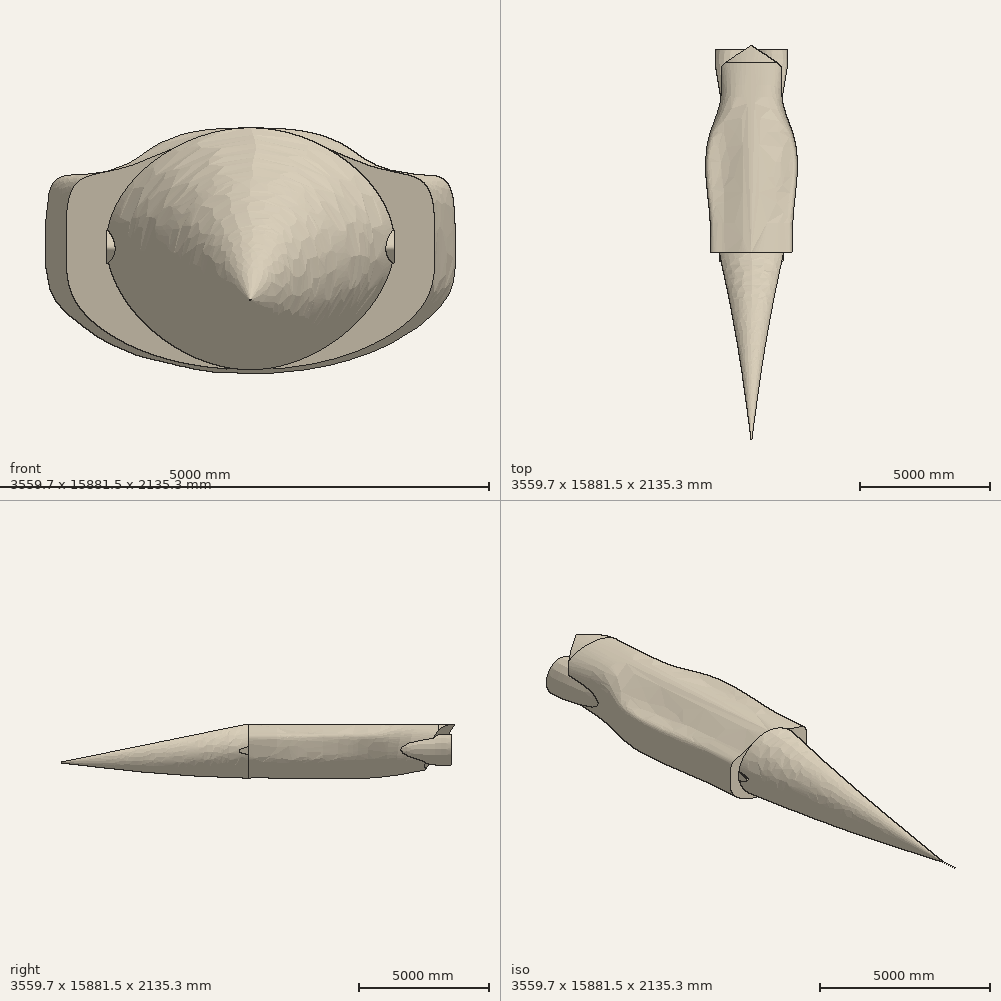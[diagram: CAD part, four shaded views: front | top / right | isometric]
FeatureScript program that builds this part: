
annotation { "Feature Type Name" : "Feature", "Feature Type Description" : "" }
export const myFeature = defineFeature(function(context is Context, id is Id, definition is map)
    precondition{}
    {
        {
            var Q0;
            Q0=qCreatedBy(makeId("Right.planeOp"),FACE);
            var sketch = newSketch(context, id + "F0", { "sketchPlane" : qUnion([Q0])});
            skLineSegment(sketch, "E0", {"start": v(0, 0) * mm, "end": v(-1750, 0) * mm});
            skLineSegment(sketch, "E1", {"start": v(-1750, 0) * mm, "end": v(-3500, 0) * mm});
            skLineSegment(sketch, "E2", {"start": v(-3500, 0) * mm, "end": v(-3500, -1000) * mm});
            skLineSegment(sketch, "E3", {"start": v(-3500, -1000) * mm, "end": v(-8500, -1000) * mm});
            skLineSegment(sketch, "E4", {"start": v(-8500, -1000) * mm, "end": v(-8500, -499.31) * mm});
            skLineSegment(sketch, "E5", {"start": v(-1151.4, 0) * mm, "end": v(-1151.4, 1000) * mm});
            skLineSegment(sketch, "E6", {"start": v(-1151.4, 1000) * mm, "end": v(-8500, -499.31) * mm});
            skLineSegment(sketch, "E7", {"start": v(-8500, -499.31) * mm, "end": v(-3500, -1000) * mm});
            skLineSegment(sketch, "E8", {"start": v(-3500, 0) * mm, "end": v(-3500, 520.82) * mm});
            skLineSegment(sketch, "E9", {"start": v(-8500, -499.31) * mm, "end": v(-8450, -499.31) * mm});
            skLineSegment(sketch, "E10", {"start": v(-8450, -499.31) * mm, "end": v(-8450, -489.1) * mm});
            skLineSegment(sketch, "E11", {"start": v(-8450, -499.31) * mm, "end": v(-8450, -504.32) * mm});
            skSolve(sketch);
        }
        {
            var Q0;
            Q0=sQuery(id+"F0.wireOp",EDGE,"E5");
            cPlane(context, id + "F1", {"entities" : qUnion([Q0]), "cplaneType" : CPlaneType.LINE_ANGLE, "offset" : 25 * mm, "angle" : 90 * degree, "oppositeDirection" : true, "width" : 150 * mm, "height" : 150 * mm});
        }
        {
            var Q0;
            Q0=qCreatedBy(id+"F1.planeOp",FACE);
            var sketch = newSketch(context, id + "F2", { "sketchPlane" : qUnion([Q0])});
            skPoint(sketch, "E12.middle", {"position": v(0, 0) * mm});
            skFitSpline(sketch, "E13", {"points": [v(0, 1000) * mm, v(-1060, 662.5) * mm, v(-1517.6, 506.84) * mm, v(-1600, 0) * mm, v(-1517.6, -506.84) * mm, v(-750, -1000) * mm, v(750, -1000) * mm, v(1517.6, -506.84) * mm, v(1600, 0) * mm, v(1517.6, 506.84) * mm, v(1060, 662.5) * mm, v(0, 1000) * mm]});
            skSolve(sketch);
        }
        {
            var Q0;
            Q0=qCreatedBy(makeId("Front.planeOp"),FACE);
            var sketch = newSketch(context, id + "F3", { "sketchPlane" : qUnion([Q0])});
            skPoint(sketch, "E14.middle", {"position": v(0, 0) * mm});
            skFitSpline(sketch, "E15", {"points": [v(0, 1000) * mm, v(-1060, 662.5) * mm, v(-1517.6, 506.84) * mm, v(-1600, 0) * mm, v(-1517.6, -506.84) * mm, v(-750, -1000) * mm, v(750, -1000) * mm, v(1517.6, -506.84) * mm, v(1600, 0) * mm, v(1517.6, 506.84) * mm, v(1060, 662.5) * mm, v(0, 1000) * mm]});
            skSolve(sketch);
        }
        {
            var Q0;
            Q0=qCreatedBy(makeId("Front.planeOp"),FACE);
            cPlane(context, id + "F4", {"entities" : qUnion([Q0]), "cplaneType" : CPlaneType.OFFSET, "offset" : 3500 * mm, "oppositeDirection" : true, "width" : 150 * mm, "height" : 150 * mm});
        }
        {
            var Q0;
            Q0=qCreatedBy(id+"F4.planeOp",FACE);
            var sketch = newSketch(context, id + "F5", { "sketchPlane" : qUnion([Q0])});
            skPoint(sketch, "E16.middle", {"position": v(0, 0) * mm});
            skFitSpline(sketch, "E17", {"points": [v(0, 1000) * mm, v(-1060, 662.5) * mm, v(-1517.6, 506.84) * mm, v(-1600, 0) * mm, v(-1517.6, -506.84) * mm, v(-750, -1000) * mm, v(750, -1000) * mm, v(1517.6, -506.84) * mm, v(1600, 0) * mm, v(1517.6, 506.84) * mm, v(1060, 662.5) * mm, v(0, 1000) * mm]});
            skSolve(sketch);
        }
        {
            var Q0;
            Q0=qCreatedBy(makeId("Front.planeOp"),FACE);
            cPlane(context, id + "F6", {"entities" : qUnion([Q0]), "cplaneType" : CPlaneType.OFFSET, "offset" : 4500 * mm, "oppositeDirection" : true, "width" : 150 * mm, "height" : 150 * mm});
        }
        {
            var Q0;
            Q0=qCreatedBy(id+"F6.planeOp",FACE);
            var sketch = newSketch(context, id + "F7", { "sketchPlane" : qUnion([Q0])});
            skPoint(sketch, "E18.middle", {"position": v(0, 0) * mm});
            skFitSpline(sketch, "E19", {"points": [v(0, 1000) * mm, v(-1060, 662.5) * mm, v(-1250, 0) * mm, v(-1060, -662.5) * mm, v(0, -1000) * mm, v(1060, -662.5) * mm, v(1250, 0) * mm, v(1060, 662.5) * mm, v(0, 1000) * mm]});
            skSolve(sketch);
        }
        {
            var Q0;
            Q0=qCreatedBy(makeId("Front.planeOp"),FACE);
            cPlane(context, id + "F8", {"entities" : qUnion([Q0]), "cplaneType" : CPlaneType.OFFSET, "offset" : 6232.05 * mm, "oppositeDirection" : true, "width" : 150 * mm, "height" : 150 * mm});
        }
        {
            var Q0;
            Q0=qCreatedBy(id+"F8.planeOp",FACE);
            var sketch = newSketch(context, id + "F9", { "sketchPlane" : qUnion([Q0])});
            skPoint(sketch, "E20.middle", {"position": v(0, 0) * mm});
            skFitSpline(sketch, "E21", {"points": [v(0, 1000) * mm, v(-1060, 662.5) * mm, v(-1250, 0) * mm, v(-848, -530) * mm, v(848, -530) * mm, v(1250, 0) * mm, v(1060, 662.5) * mm, v(0, 1000) * mm]});
            skSolve(sketch);
        }
        {
            var Q0;
            Q0=makeQuery(id+"F2.imprint","IMPRINT",FACE,{"disambiguationData":[TD([[makeQuery(id+"F2.imprint","IMPRINT",EDGE,{"derivedFrom":sQuery(id+"F2.wireOp",EDGE,"E13")}),1.0]])]});
            var Q1;
            Q1=makeQuery(id+"F3.imprint","IMPRINT",FACE,{"disambiguationData":[TD([[makeQuery(id+"F3.imprint","IMPRINT",EDGE,{"derivedFrom":sQuery(id+"F3.wireOp",EDGE,"E15")}),1.0]])]});
            var Q2;
            Q2=makeQuery(id+"F5.imprint","IMPRINT",FACE,{"disambiguationData":[TD([[makeQuery(id+"F5.imprint","IMPRINT",EDGE,{"derivedFrom":sQuery(id+"F5.wireOp",EDGE,"E17")}),1.0]])]});
            var Q3;
            Q3=makeQuery(id+"F7.imprint","IMPRINT",FACE,{"disambiguationData":[TD([[makeQuery(id+"F7.imprint","IMPRINT",EDGE,{"derivedFrom":sQuery(id+"F7.wireOp",EDGE,"E19")}),1.0]])]});
            var Q4;
            Q4=makeQuery(id+"F9.imprint","IMPRINT",FACE,{"disambiguationData":[TD([[makeQuery(id+"F9.imprint","IMPRINT",EDGE,{"derivedFrom":sQuery(id+"F9.wireOp",EDGE,"E21")}),1.0]])]});
            loft(context, id + "F10", {"sheetProfilesArray" : [{ "sheetProfileEntities" : qUnion([Q0]) }, { "sheetProfileEntities" : qUnion([Q1]) }, { "sheetProfileEntities" : qUnion([Q2]) }, { "sheetProfileEntities" : qUnion([Q3]) }, { "sheetProfileEntities" : qUnion([Q4]) }]});
        }
        {
            var Q0;
            Q0=makeQuery(id+"F10.opLoft","CAP_FACE",FACE,{"disambiguationData":[OSD([makeQuery(id+"F9.imprint","IMPRINT",FACE,{"disambiguationData":[TD([[makeQuery(id+"F9.imprint","IMPRINT",EDGE,{"derivedFrom":sQuery(id+"F9.wireOp",EDGE,"E21")}),1.0]])]})])],"isStart":true});
            extrude(context, id + "F11", {"entities" : qUnion([Q0]), "operationType" : NewBodyOperationType.ADD, "depth" : 649.4 * mm, "offsetDistance" : 25 * mm});
        }
        {
            var Q0;
            Q0=qCreatedBy(makeId("Right.planeOp"),FACE);
            var sketch = newSketch(context, id + "F12", { "sketchPlane" : qUnion([Q0])});
            skLineSegment(sketch, "E22", {"start": v(0, 0) * mm, "end": v(4500, 0) * mm});
            skLineSegment(sketch, "E23", {"start": v(4500, 0) * mm, "end": v(6232.05, 0) * mm});
            skLineSegment(sketch, "E24", {"start": v(4500, 0) * mm, "end": v(4500, 1000) * mm});
            skLineSegment(sketch, "E25", {"start": v(4500, 1000) * mm, "end": v(6881.46, 1000) * mm});
            skLineSegment(sketch, "E26", {"start": v(6881.46, 1000) * mm, "end": v(6881.46, -1000) * mm});
            skLineSegment(sketch, "E27", {"start": v(6881.46, 1000) * mm, "end": v(6232.05, 0) * mm});
            skLineSegment(sketch, "E28", {"start": v(6232.05, 0) * mm, "end": v(5582.64, -1000) * mm});
            skLineSegment(sketch, "E29", {"start": v(5582.64, -1000) * mm, "end": v(6881.46, -1000) * mm});
            skSolve(sketch);
        }
        {
            var Q0;
            Q0=makeQuery(id+"F12.imprint","IMPRINT",FACE,{"disambiguationData":[TD([[makeQuery(id+"F12.imprint","IMPRINT",EDGE,{"derivedFrom":sQuery(id+"F12.wireOp",EDGE,"E26")}),-1.0]])]});
            var Q1;
            Q1=sQuery(id+"F12.wireOp",EDGE,"E25");
            revolve(context, id + "F13", {"operationType" : NewBodyOperationType.REMOVE, "entities" : qUnion([Q0]), "axis" : qUnion([Q1]), "revolveType" : RevolveType.SYMMETRIC, "oppositeDirection" : true, "angle" : 182 * degree});
        }
        {
            var Q0;
            Q0=qCreatedBy(id+"F1.planeOp",FACE);
            var sketch = newSketch(context, id + "F14", { "sketchPlane" : qUnion([Q0])});
            skFitSpline(sketch, "E30", {"points": [v(0, 1000) * mm, v(-1250, 0) * mm, v(0, -1099.92) * mm, v(1250, 0) * mm, v(0, 1000) * mm]});
            skSolve(sketch);
        }
        {
            var Q0;
            Q0=qCreatedBy(makeId("Front.planeOp"),FACE);
            cPlane(context, id + "F15", {"entities" : qUnion([Q0]), "cplaneType" : CPlaneType.OFFSET, "offset" : 3500 * mm, "width" : 150 * mm, "height" : 150 * mm});
        }
        {
            var Q0;
            Q0=qCreatedBy(id+"F15.planeOp",FACE);
            var sketch = newSketch(context, id + "F16", { "sketchPlane" : qUnion([Q0])});
            skCircle(sketch, "E31", {"center": v(0, -239.59) * mm, "radius": 760.41 * mm});
            skSolve(sketch);
        }
        {
            var Q0;
            Q0=qCreatedBy(makeId("Front.planeOp"),FACE);
            cPlane(context, id + "F17", {"entities" : qUnion([Q0]), "cplaneType" : CPlaneType.OFFSET, "offset" : 8450 * mm, "width" : 150 * mm, "height" : 150 * mm});
        }
        {
            var Q0;
            Q0=qCreatedBy(id+"F17.planeOp",FACE);
            var sketch = newSketch(context, id + "F18", { "sketchPlane" : qUnion([Q0])});
            skCircle(sketch, "E32", {"center": v(0, -496.71) * mm, "radius": 7.6 * mm});
            skSolve(sketch);
        }
        {
            var Q1;
            Q1=makeQuery(id+"F18.imprint","IMPRINT",FACE,{"disambiguationData":[TD([[makeQuery(id+"F18.imprint","IMPRINT",EDGE,{"derivedFrom":sQuery(id+"F18.wireOp",EDGE,"E32")}),1.0]])]});
            var Q2;
            Q2=makeQuery(id+"F16.imprint","IMPRINT",FACE,{"disambiguationData":[TD([[makeQuery(id+"F16.imprint","IMPRINT",EDGE,{"derivedFrom":sQuery(id+"F16.wireOp",EDGE,"E31")}),1.0]])]});
            var Q3;
            Q3=makeQuery(id+"F14.imprint","IMPRINT",FACE,{"disambiguationData":[TD([[makeQuery(id+"F14.imprint","IMPRINT",EDGE,{"derivedFrom":sQuery(id+"F14.wireOp",EDGE,"E30")}),1.0]])]});
            loft(context, id + "F19", {"operationType" : NewBodyOperationType.ADD, "sheetProfilesArray" : [{ "sheetProfileEntities" : qUnion([Q1]) }, { "sheetProfileEntities" : qUnion([Q2]) }, { "sheetProfileEntities" : qUnion([Q3]) }]});
        }
        {
            var Q0;
            Q0=makeQuery(id+"F19.opLoft","CAP_FACE",FACE,{"disambiguationData":[OSD([makeQuery(id+"F18.imprint","IMPRINT",FACE,{"disambiguationData":[TD([[makeQuery(id+"F18.imprint","IMPRINT",EDGE,{"derivedFrom":sQuery(id+"F18.wireOp",EDGE,"E32")}),1.0]])]})])],"isStart":true});
            extrude(context, id + "F20", {"entities" : qUnion([Q0]), "operationType" : NewBodyOperationType.ADD, "depth" : 550 * mm, "offsetDistance" : 25 * mm});
        }
        {
            var Q0;
            Q0=qCreatedBy(makeId("Front.planeOp"),FACE);
            cPlane(context, id + "F21", {"entities" : qUnion([Q0]), "cplaneType" : CPlaneType.OFFSET, "offset" : 3500 * mm, "oppositeDirection" : true, "width" : 150 * mm, "height" : 150 * mm});
        }
        {
            var Q0;
            Q0=qCreatedBy(id+"F21.planeOp",FACE);
            var sketch = newSketch(context, id + "F22", { "sketchPlane" : qUnion([Q0])});
            skCircle(sketch, "E33", {"center": v(-800, 0) * mm, "radius": 600 * mm});
            skCircle(sketch, "E34", {"center": v(800, 0) * mm, "radius": 600 * mm});
            skSolve(sketch);
        }
        {
            var Q0;
            Q0=qCreatedBy(makeId("Front.planeOp"),FACE);
            cPlane(context, id + "F23", {"entities" : qUnion([Q0]), "cplaneType" : CPlaneType.OFFSET, "offset" : 4500 * mm, "oppositeDirection" : true, "width" : 150 * mm, "height" : 150 * mm});
        }
        {
            var Q0;
            Q0=qCreatedBy(id+"F23.planeOp",FACE);
            var sketch = newSketch(context, id + "F24", { "sketchPlane" : qUnion([Q0])});
            skCircle(sketch, "E35", {"center": v(-800, 0) * mm, "radius": 400 * mm});
            skCircle(sketch, "E36", {"center": v(800, 0) * mm, "radius": 400 * mm});
            skSolve(sketch);
        }
        {
            var Q0;
            Q0=qCreatedBy(makeId("Front.planeOp"),FACE);
            cPlane(context, id + "F25", {"entities" : qUnion([Q0]), "cplaneType" : CPlaneType.OFFSET, "offset" : 6232.05 * mm, "oppositeDirection" : true, "width" : 150 * mm, "height" : 150 * mm});
        }
        {
            var Q0;
            Q0=qCreatedBy(id+"F25.planeOp",FACE);
            var sketch = newSketch(context, id + "F26", { "sketchPlane" : qUnion([Q0])});
            skCircle(sketch, "E37", {"center": v(-800, 0) * mm, "radius": 600 * mm});
            skCircle(sketch, "E38", {"center": v(800, 0) * mm, "radius": 600 * mm});
            skSolve(sketch);
        }
        {
            var Q0;
            Q0=qCreatedBy(makeId("Front.planeOp"),FACE);
            cPlane(context, id + "F27", {"entities" : qUnion([Q0]), "cplaneType" : CPlaneType.OFFSET, "offset" : 6732.05 * mm, "oppositeDirection" : true, "width" : 150 * mm, "height" : 150 * mm});
        }
        {
            var Q0;
            Q0=qCreatedBy(id+"F27.planeOp",FACE);
            var sketch = newSketch(context, id + "F28", { "sketchPlane" : qUnion([Q0])});
            skCircle(sketch, "E39", {"center": v(-800, 0) * mm, "radius": 600 * mm});
            skCircle(sketch, "E40", {"center": v(800, 0) * mm, "radius": 600 * mm});
            skSolve(sketch);
        }
        {
            var Q0;
            Q0=makeQuery(id+"F22.imprint","IMPRINT",FACE,{"disambiguationData":[TD([[makeQuery(id+"F22.imprint","IMPRINT",EDGE,{"derivedFrom":sQuery(id+"F22.wireOp",EDGE,"E33")}),1.0]])]});
            var Q1;
            Q1=makeQuery(id+"F24.imprint","IMPRINT",FACE,{"disambiguationData":[TD([[makeQuery(id+"F24.imprint","IMPRINT",EDGE,{"derivedFrom":sQuery(id+"F24.wireOp",EDGE,"E35")}),1.0]])]});
            var Q2;
            Q2=makeQuery(id+"F26.imprint","IMPRINT",FACE,{"disambiguationData":[TD([[makeQuery(id+"F26.imprint","IMPRINT",EDGE,{"derivedFrom":sQuery(id+"F26.wireOp",EDGE,"E37")}),1.0]])]});
            var Q3;
            Q3=makeQuery(id+"F28.imprint","IMPRINT",FACE,{"disambiguationData":[TD([[makeQuery(id+"F28.imprint","IMPRINT",EDGE,{"derivedFrom":sQuery(id+"F28.wireOp",EDGE,"E39")}),1.0]])]});
            loft(context, id + "F29", {"sheetProfilesArray" : [{ "sheetProfileEntities" : qUnion([Q0]) }, { "sheetProfileEntities" : qUnion([Q1]) }, { "sheetProfileEntities" : qUnion([Q2]) }, { "sheetProfileEntities" : qUnion([Q3]) }]});
        }
        {
            var Q0;
            Q0=makeQuery(id+"F22.imprint","IMPRINT",FACE,{"disambiguationData":[TD([[makeQuery(id+"F22.imprint","IMPRINT",EDGE,{"derivedFrom":sQuery(id+"F22.wireOp",EDGE,"E34")}),1.0]])]});
            var Q1;
            Q1=makeQuery(id+"F24.imprint","IMPRINT",FACE,{"disambiguationData":[TD([[makeQuery(id+"F24.imprint","IMPRINT",EDGE,{"derivedFrom":sQuery(id+"F24.wireOp",EDGE,"E36")}),1.0]])]});
            var Q2;
            Q2=makeQuery(id+"F26.imprint","IMPRINT",FACE,{"disambiguationData":[TD([[makeQuery(id+"F26.imprint","IMPRINT",EDGE,{"derivedFrom":sQuery(id+"F26.wireOp",EDGE,"E38")}),1.0]])]});
            var Q3;
            Q3=makeQuery(id+"F28.imprint","IMPRINT",FACE,{"disambiguationData":[TD([[makeQuery(id+"F28.imprint","IMPRINT",EDGE,{"derivedFrom":sQuery(id+"F28.wireOp",EDGE,"E40")}),1.0]])]});
            loft(context, id + "F30", {"sheetProfilesArray" : [{ "sheetProfileEntities" : qUnion([Q0]) }, { "sheetProfileEntities" : qUnion([Q1]) }, { "sheetProfileEntities" : qUnion([Q2]) }, { "sheetProfileEntities" : qUnion([Q3]) }]});
        }
        {
            var Q0;
            Q0=qCreatedBy(makeId("Right.planeOp"),FACE);
            var sketch = newSketch(context, id + "F31", { "sketchPlane" : qUnion([Q0])});
            skFitSpline(sketch, "E41", {"points": [v(-1500, -50) * mm, v(0, 250) * mm, v(3000, 0) * mm, v(0, -250) * mm, v(-1500, -50) * mm]});
            skSolve(sketch);
        }
        {
            var Q0;
            Q0=qSketchRegion(id+"F31",true);
            extrude(context, id + "F32", {"entities" : qUnion([Q0]), "endBound" : BoundingType.SYMMETRIC, "depth" : 2500 * mm, "offsetDistance" : 25 * mm});
        }
    });
